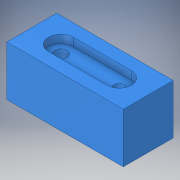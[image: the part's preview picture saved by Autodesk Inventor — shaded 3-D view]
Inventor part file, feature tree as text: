
AUTODESK INVENTOR PART (.ipt)
format: ipt  version: 2018 (Build 220112000, 112)  size: 137,216 bytes
history: native  units: in
note: dims shown in document units (in); Inventor stores cm internally (conversion verified against a paired STEP export)
features: extrude x4, sketch x3, projected_geometry x2
ambient origin geometry x8: Origin, YZ Plane, XZ Plane, XY Plane, X Axis, Y Axis, Z Axis, Center Point
bodies: Body1 (feature_tree)
feature tree (9):
  extrude  "Extrusion5"  Depth=3.5in
  sketch  "Sketch10"  dims[d20=0.3125in d21=1.0in]
  extrude  "Extrusion8"  Depth=1.0in
  extrude  "Extrusion9"  Depth=0.875in
  extrude  "Extrusion10"  Depth=1.5in TaperAngle=0.0deg
  sketch  "Sketch1"  dims[d3=1.5in d4=3.5in]
  projected_geometry  "Projected Loop7"
  sketch  "Sketch12"  dims[d22=0.875in d23=0.875in d24=1.5in d25=0.0in d38=0.38in d39=0.75in d40=0.0in d41=0.75in d42=0.25in d43=0.0in d44=0.5in d45=0.0in]
  projected_geometry  "Projected Loop8"
